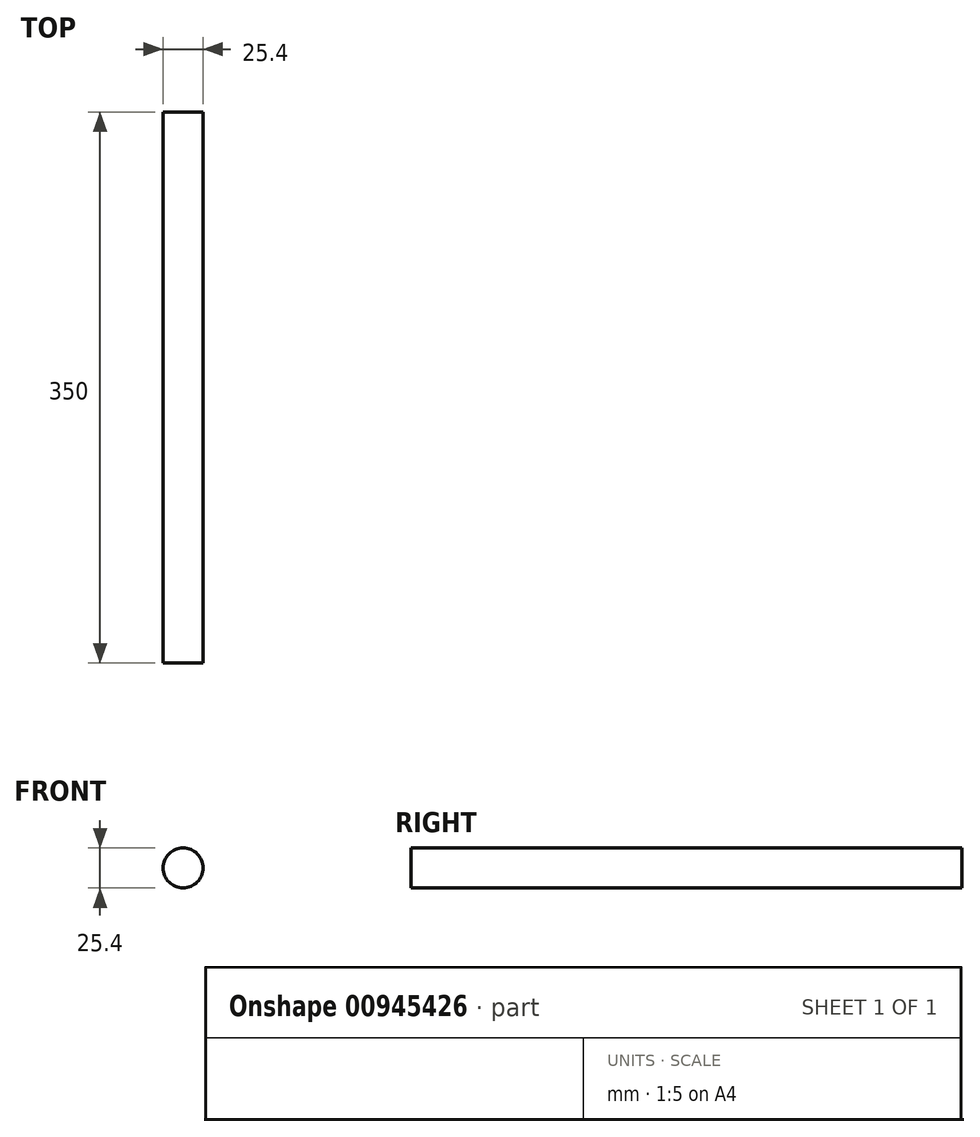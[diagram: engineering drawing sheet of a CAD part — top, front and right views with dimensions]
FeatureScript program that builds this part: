
annotation { "Feature Type Name" : "Feature", "Feature Type Description" : "" }
export const myFeature = defineFeature(function(context is Context, id is Id, definition is map)
    precondition{}
    {
        {
            var Q0;
            Q0=qCreatedBy(makeId("Front.planeOp"),FACE);
            var sketch = newSketch(context, id + "F0", { "sketchPlane" : qUnion([Q0])});
            skCircle(sketch, "E0", {"center": v(0, 0) * mm, "radius": 12.7 * mm});
            skSolve(sketch);
        }
        {
            var Q0;
            Q0=sQuery(id+"F0.wireOp",EDGE,"E0");
            extrude(context, id + "F1", {"bodyType" : ToolBodyType.SURFACE, "surfaceEntities" : qUnion([Q0]), "depth" : 350 * mm, "offsetDistance" : 25.4 * mm});
        }
    });
